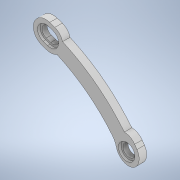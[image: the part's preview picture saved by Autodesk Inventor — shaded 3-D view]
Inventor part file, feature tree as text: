
AUTODESK INVENTOR PART (.ipt)
format: ipt  version: 2020.3 (Build 243373000, 373)  size: 235,520 bytes
history: native  units: mm
features: extrude x8, sketch x6, projected_geometry x5, plane x1, fillet x1
ambient origin geometry x8: Origin, YZ Plane, XZ Plane, XY Plane, X Axis, Y Axis, Z Axis, Center Point
bodies: Solid1 (feature_tree)
feature tree (21):
  plane  "Work Plane1"
  extrude  "Extrusion2"  Depth=3.0mm TaperAngle=0.0deg
  extrude  "Extrusion4"  Depth=5.0mm TaperAngle=0.0deg
  sketch  "Sketch5"  dims[d15=10.0mm d18=5.0mm]
  extrude  "Extrusion5"  Depth=5.0mm
  sketch  "Sketch6"  dims[d19=5.0mm d20=10.0mm d21=0.0mm]
  extrude  "Extrusion6"  Depth=10.0mm TaperAngle=0.0deg
  extrude  "Extrusion7"  Depth=10.0mm TaperAngle=0.0deg
  extrude  "Extrusion8"  Depth=1.0mm
  extrude  "Extrusion9"  Depth=1.0mm
  extrude  "Extrusion10"  Depth=4.0mm
  fillet  "Fillet1"  Radius=1.0mm
  sketch  "Sketch2"  dims[d3=60.0mm d4=3.0mm d5=0.0mm]
  projected_geometry  "Projected Loop1"
  projected_geometry  "Projected Loop2"
  sketch  "Sketch4"  dims[d10=3.0mm d11=0.0mm d13=5.0mm d14=0.0mm]
  projected_geometry  "Projected Loop4"
  projected_geometry  "Projected Loop5"
  sketch  "Sketch7"  dims[d22=10.0mm d27=10.0mm d28=0.0mm]
  sketch  "Sketch8"  dims[d29=0.261799mm d30=1.0mm d31=1.0mm d32=6.6mm d33=1.0mm d34=0.0mm d35=0.8mm d36=1.0mm d37=0.0mm d38=10.0mm d39=0.0mm d40=4.0mm]
  projected_geometry  "Projected Loop8"
